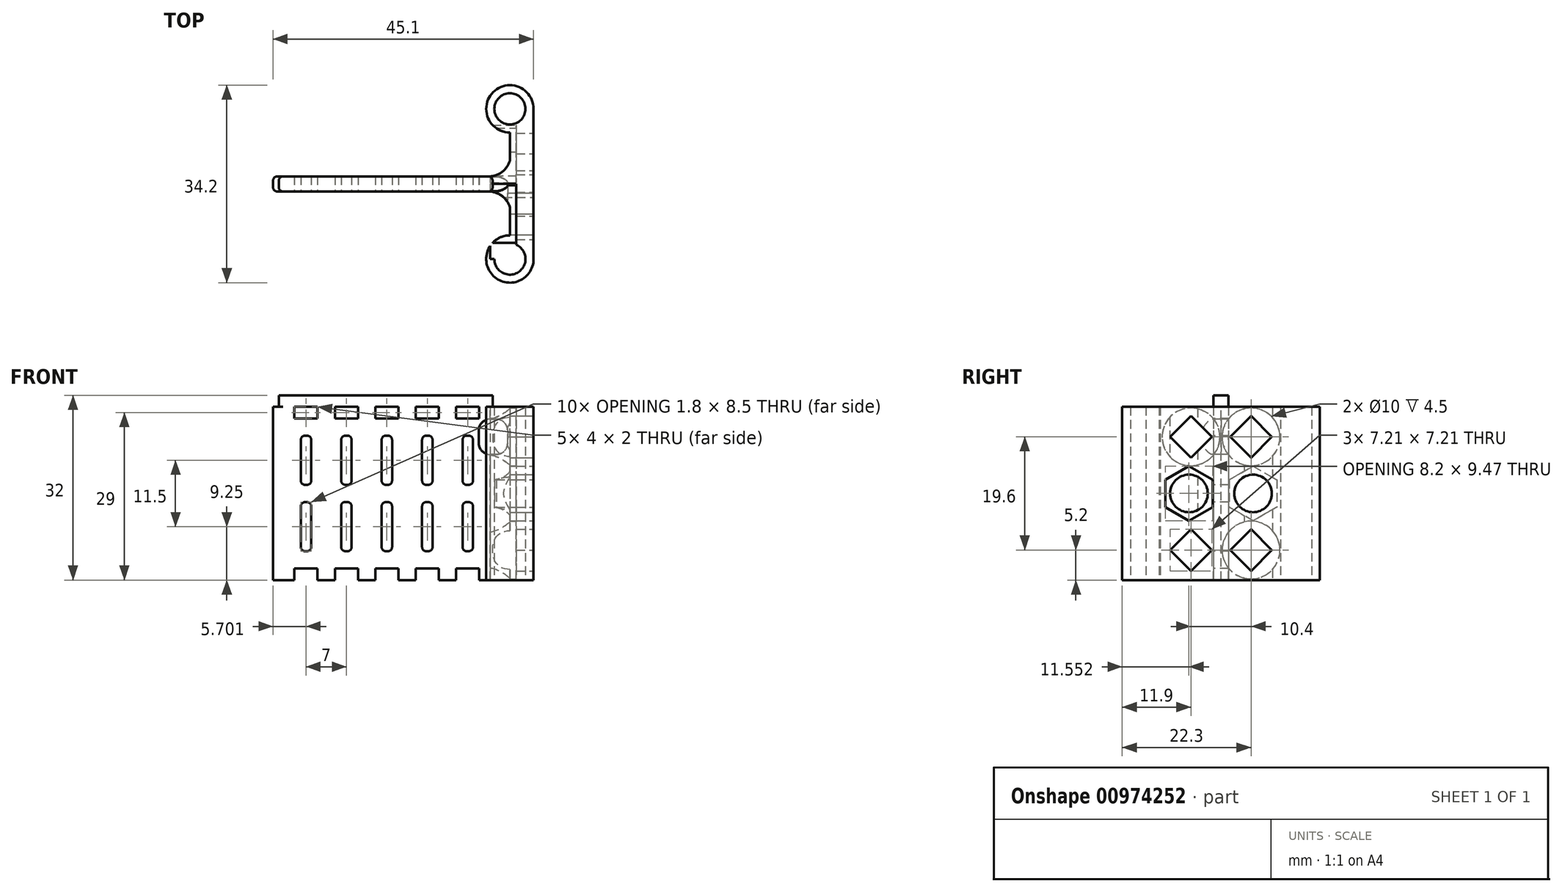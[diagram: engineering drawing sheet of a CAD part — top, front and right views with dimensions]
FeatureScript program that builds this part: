
annotation { "Feature Type Name" : "Feature", "Feature Type Description" : "" }
export const myFeature = defineFeature(function(context is Context, id is Id, definition is map)
    precondition{}
    {
        {
            var Q0;
            Q0=qCreatedBy(makeId("Top.planeOp"),FACE);
            var sketch = newSketch(context, id + "F0", { "sketchPlane" : qUnion([Q0])});
            skLineSegment(sketch, "E0", {"start": v(14.18, 21.66) * mm, "end": v(14.18, -4.34) * mm, "construction": true});
            skPoint(sketch, "E1", {"position": v(14.18, 8.66) * mm});
            skCircle(sketch, "E2", {"center": v(14.18, 21.66) * mm, "radius": 2.7 * mm});
            skCircle(sketch, "E3", {"center": v(14.18, -4.34) * mm, "radius": 2.7 * mm});
            skCircle(sketch, "E4", {"center": v(14.18, 21.66) * mm, "radius": 4.1 * mm});
            skCircle(sketch, "E5", {"center": v(14.18, -4.34) * mm, "radius": 4.1 * mm});
            skLineSegment(sketch, "E6", {"start": v(14.18, 26.11) * mm, "end": v(14.18, -8.89) * mm, "construction": true});
            skLineSegment(sketch, "E7", {"start": v(-25.82, 8.66) * mm, "end": v(11.18, 8.66) * mm, "construction": true});
            skLineSegment(sketch, "E8.0", {"start": v(-25.12, 7.36) * mm, "end": v(10.48, 7.36) * mm});
            skLineSegment(sketch, "E9.0", {"start": v(-25.12, 9.96) * mm, "end": v(10.48, 9.96) * mm});
            skLineSegment(sketch, "E10", {"start": v(-25.82, 9.26) * mm, "end": v(-25.82, 8.06) * mm});
            skLineSegment(sketch, "E11", {"start": v(11.18, 9.26) * mm, "end": v(11.18, 8.06) * mm});
            skLineSegment(sketch, "E12", {"start": v(11.18, 8.66) * mm, "end": v(14.18, 8.66) * mm, "construction": true});
            skPoint(sketch, "E13.visualSharp", {"position": v(11.18, 9.96) * mm});
            skArc(sketch, "E13.filletArc", {"start": v(11.18, 9.26) * mm, "mid": v(10.98, 9.76) * mm, "end": v(10.48, 9.96) * mm});
            skPoint(sketch, "E14.visualSharp", {"position": v(11.18, 7.36) * mm});
            skArc(sketch, "E14.filletArc", {"start": v(10.48, 7.36) * mm, "mid": v(10.98, 7.57) * mm, "end": v(11.18, 8.06) * mm});
            skPoint(sketch, "E15.visualSharp", {"position": v(-25.82, 9.96) * mm});
            skArc(sketch, "E15.filletArc", {"start": v(-25.12, 9.96) * mm, "mid": v(-25.61, 9.76) * mm, "end": v(-25.82, 9.26) * mm});
            skPoint(sketch, "E16.visualSharp", {"position": v(-25.82, 7.36) * mm});
            skArc(sketch, "E16.filletArc", {"start": v(-25.82, 8.06) * mm, "mid": v(-25.61, 7.57) * mm, "end": v(-25.12, 7.36) * mm});
            skLineSegment(sketch, "E17", {"start": v(18.28, 21.66) * mm, "end": v(18.28, -4.34) * mm});
            skLineSegment(sketch, "E18", {"start": v(14.18, 17.56) * mm, "end": v(14.18, -0.24) * mm});
            skPoint(sketch, "E19.startSnap0", {"position": v(13.1, 10.4) * mm});
            skArc(sketch, "E20", {"start": v(14.18, 4.62) * mm, "mid": v(12.78, 6.6) * mm, "end": v(10.48, 7.36) * mm});
            skArc(sketch, "E21.MirrorCS", {"start": v(14.18, 12.7) * mm, "mid": v(12.78, 10.72) * mm, "end": v(10.48, 9.96) * mm});
            skLineSegment(sketch, "E22.0", {"start": v(-26.82, 9.26) * mm, "end": v(-26.82, 8.06) * mm});
            skLineSegment(sketch, "E23", {"start": v(-25.12, 7.36) * mm, "end": v(-26.12, 7.36) * mm});
            skLineSegment(sketch, "E24", {"start": v(-25.12, 9.96) * mm, "end": v(-26.12, 9.96) * mm});
            skPoint(sketch, "E25.visualSharp", {"position": v(-26.82, 7.36) * mm});
            skArc(sketch, "E25.filletArc", {"start": v(-26.82, 8.06) * mm, "mid": v(-26.61, 7.57) * mm, "end": v(-26.12, 7.36) * mm});
            skPoint(sketch, "E26.visualSharp", {"position": v(-26.82, 9.96) * mm});
            skArc(sketch, "E26.filletArc", {"start": v(-26.12, 9.96) * mm, "mid": v(-26.61, 9.76) * mm, "end": v(-26.82, 9.26) * mm});
            skSolve(sketch);
        }
        {
            var Q0;
            Q0=qSketchRegion(id+"F0",true);
            extrude(context, id + "F1", {"entities" : qUnion([Q0]), "depth" : 30 * mm, "offsetDistance" : 25 * mm});
        }
        {
            var Q0;
            Q0=makeQuery(id+"F1.opExtrude","CAP_FACE",FACE,{"disambiguationData":[OSD([sQuery(id+"F0.wireOp",EDGE,"E2"),sQuery(id+"F0.wireOp",EDGE,"E3"),sQuery(id+"F0.wireOp",EDGE,"E4"),sQuery(id+"F0.wireOp",EDGE,"E5"),sQuery(id+"F0.wireOp",EDGE,"5XY8Sy6J-rJSc-VVxI-sy8d-kj6zddSfZvcS"),sQuery(id+"F0.wireOp",EDGE,"L47yK2bG-XMTy-tZuv-y9jX-F6sUyB3i6wNF"),sQuery(id+"F0.wireOp",EDGE,"E8.0"),sQuery(id+"F0.wireOp",EDGE,"E9.0"),sQuery(id+"F0.wireOp",EDGE,"E10"),sQuery(id+"F0.wireOp",EDGE,"E15.filletArc"),sQuery(id+"F0.wireOp",EDGE,"E16.filletArc"),sQuery(id+"F0.wireOp",EDGE,"fYA9DaEY-N4rZ-RQXs-IzNy-WeN906tYVGf5"),sQuery(id+"F0.wireOp",EDGE,"5c931c3b-5688-4883-9c1d-30dd6726151f0.MirrorCS")])],"isStart":false});
            var sketch = newSketch(context, id + "F2", { "sketchPlane" : qUnion([Q0])});
            skArc(sketch, "E27.0", {"start": v(11.18, 9.26) * mm, "mid": v(10.98, 9.76) * mm, "end": v(10.48, 9.96) * mm});
            skLineSegment(sketch, "E27.1", {"start": v(11.18, 9.26) * mm, "end": v(11.18, 8.06) * mm});
            skArc(sketch, "E27.2", {"start": v(10.48, 7.36) * mm, "mid": v(10.98, 7.57) * mm, "end": v(11.18, 8.06) * mm});
            skLineSegment(sketch, "E27.3", {"start": v(-25.12, 7.36) * mm, "end": v(10.48, 7.36) * mm});
            skLineSegment(sketch, "E27.4", {"start": v(-25.12, 9.96) * mm, "end": v(10.48, 9.96) * mm});
            skArc(sketch, "E27.5", {"start": v(-25.12, 9.96) * mm, "mid": v(-25.61, 9.76) * mm, "end": v(-25.82, 9.26) * mm});
            skLineSegment(sketch, "E27.6", {"start": v(-25.82, 9.26) * mm, "end": v(-25.82, 8.06) * mm});
            skArc(sketch, "E27.7", {"start": v(-25.82, 8.06) * mm, "mid": v(-25.61, 7.57) * mm, "end": v(-25.12, 7.36) * mm});
            skSolve(sketch);
        }
        {
            var Q0;
            Q0=makeQuery(id+"F2.imprint","IMPRINT",FACE,{"disambiguationData":[TD([[makeQuery(id+"F2.imprint","IMPRINT",EDGE,{"derivedFrom":sQuery(id+"F2.wireOp",EDGE,"E27.0")}),1.0]])]});
            extrude(context, id + "F3", {"entities" : qUnion([Q0]), "operationType" : NewBodyOperationType.ADD, "depth" : 2 * mm, "offsetDistance" : 25 * mm});
        }
        {
            var Q0;
            Q0=makeQuery(id+"F1.opExtrude","SWEPT_FACE",FACE,{"disambiguationData":[OSD([sQuery(id+"F0.wireOp",EDGE,"E17")])]});
            var sketch = newSketch(context, id + "F4", { "sketchPlane" : qUnion([Q0])});
            skCircle(sketch, "E28", {"center": v(14.2, 15) * mm, "radius": 3.25 * mm});
            skCircle(sketch, "E29.cCircle", {"center": v(14.2, 15) * mm, "radius": 4.1 * mm, "construction": true});
            skLineSegment(sketch, "E29.0", {"start": v(10.1, 12.63) * mm, "end": v(10.1, 17.37) * mm});
            skLineSegment(sketch, "E29.1", {"start": v(10.1, 17.37) * mm, "end": v(14.2, 19.74) * mm});
            skLineSegment(sketch, "E29.2", {"start": v(14.2, 19.74) * mm, "end": v(18.3, 17.37) * mm});
            skLineSegment(sketch, "E29.3", {"start": v(18.3, 17.37) * mm, "end": v(18.3, 12.63) * mm});
            skLineSegment(sketch, "E29.4", {"start": v(18.3, 12.63) * mm, "end": v(14.2, 10.27) * mm});
            skLineSegment(sketch, "E29.5", {"start": v(14.2, 10.27) * mm, "end": v(10.1, 12.63) * mm});
            skPoint(sketch, "E29.0.midPoint", {"position": v(10.1, 15) * mm});
            skCircle(sketch, "E30", {"center": v(13.86, 24.8) * mm, "radius": 5 * mm});
            skLineSegment(sketch, "E31", {"start": v(8.66, 0) * mm, "end": v(8.66, 30) * mm});
            skLineSegment(sketch, "E32.bottom", {"start": v(17.47, 24.8) * mm, "end": v(13.86, 28.4) * mm});
            skLineSegment(sketch, "E32.top", {"start": v(13.86, 21.2) * mm, "end": v(10.25, 24.8) * mm});
            skLineSegment(sketch, "E32.left", {"start": v(17.47, 24.8) * mm, "end": v(13.86, 21.2) * mm});
            skLineSegment(sketch, "E32.right", {"start": v(13.86, 28.4) * mm, "end": v(10.25, 24.8) * mm});
            skCircle(sketch, "E33.MirrorC", {"center": v(3.46, 24.8) * mm, "radius": 5 * mm});
            skLineSegment(sketch, "E34.MirrorCS", {"start": v(3.46, 28.4) * mm, "end": v(7.07, 24.8) * mm});
            skLineSegment(sketch, "E35.MirrorCS", {"start": v(-0.15, 24.8) * mm, "end": v(3.46, 21.2) * mm});
            skLineSegment(sketch, "E36.MirrorCS", {"start": v(3.46, 21.2) * mm, "end": v(7.07, 24.8) * mm});
            skLineSegment(sketch, "E37.MirrorCS", {"start": v(-0.15, 24.8) * mm, "end": v(3.46, 28.4) * mm});
            skLineSegment(sketch, "E38.MirrorCS", {"start": v(3.11, 10.27) * mm, "end": v(7.21, 12.63) * mm});
            skLineSegment(sketch, "E39.MirrorCS", {"start": v(3.11, 19.74) * mm, "end": v(-0.99, 17.37) * mm});
            skLineSegment(sketch, "E40.MirrorCS", {"start": v(-0.99, 12.63) * mm, "end": v(3.11, 10.27) * mm});
            skPoint(sketch, "E41.MirrorP", {"position": v(7.21, 15) * mm});
            skLineSegment(sketch, "E42.MirrorCS", {"start": v(7.21, 17.37) * mm, "end": v(3.11, 19.74) * mm});
            skLineSegment(sketch, "E43.MirrorCS", {"start": v(7.21, 12.63) * mm, "end": v(7.21, 17.37) * mm});
            skLineSegment(sketch, "E44.MirrorCS", {"start": v(-0.99, 17.37) * mm, "end": v(-0.99, 12.63) * mm});
            skCircle(sketch, "E45.MirrorC", {"center": v(3.11, 15) * mm, "radius": 4.1 * mm, "construction": true});
            skCircle(sketch, "E46.MirrorC", {"center": v(3.11, 15) * mm, "radius": 3.25 * mm});
            skLineSegment(sketch, "E47", {"start": v(13.86, 30) * mm, "end": v(13.86, 0) * mm, "construction": true});
            skLineSegment(sketch, "E48", {"start": v(-4.34, 15) * mm, "end": v(21.66, 15) * mm, "construction": true});
            skLineSegment(sketch, "E49.MirrorCS", {"start": v(17.47, 5.2) * mm, "end": v(13.86, 1.6) * mm});
            skLineSegment(sketch, "E50.MirrorCS", {"start": v(-0.15, 5.2) * mm, "end": v(3.46, 1.6) * mm});
            skPoint(sketch, "E51.MirrorP", {"position": v(3.46, 5.2) * mm});
            skCircle(sketch, "E52.MirrorC", {"center": v(3.46, 5.2) * mm, "radius": 5 * mm});
            skLineSegment(sketch, "E53.MirrorCS", {"start": v(17.47, 5.2) * mm, "end": v(13.86, 8.8) * mm});
            skLineSegment(sketch, "E54.MirrorCS", {"start": v(13.86, 8.8) * mm, "end": v(10.25, 5.2) * mm});
            skLineSegment(sketch, "E55.MirrorCS", {"start": v(3.46, 1.6) * mm, "end": v(7.07, 5.2) * mm});
            skPoint(sketch, "E56.MirrorP", {"position": v(13.86, 5.2) * mm});
            skCircle(sketch, "E57.MirrorC", {"center": v(13.86, 5.2) * mm, "radius": 5 * mm});
            skLineSegment(sketch, "E58.MirrorCS", {"start": v(-0.15, 5.2) * mm, "end": v(3.46, 8.8) * mm});
            skLineSegment(sketch, "E59.MirrorCS", {"start": v(3.46, 8.8) * mm, "end": v(7.07, 5.2) * mm});
            skLineSegment(sketch, "E60.MirrorCS", {"start": v(13.86, 1.6) * mm, "end": v(10.25, 5.2) * mm});
            skSolve(sketch);
        }
        {
            var Q0;
            Q0=makeQuery(id+"F4.imprint","IMPRINT",FACE,{"disambiguationData":[TD([[makeQuery(id+"F4.imprint","IMPRINT",EDGE,{"derivedFrom":sQuery(id+"F4.wireOp",EDGE,"E28")}),1.0]])]});
            var Q1;
            Q1=makeQuery(id+"F4.imprint","IMPRINT",FACE,{"disambiguationData":[TD([[makeQuery(id+"F4.imprint","IMPRINT",EDGE,{"derivedFrom":sQuery(id+"F4.wireOp",EDGE,"E34.MirrorCS")}),-1.0]])]});
            var Q2;
            Q2=makeQuery(id+"F4.imprint","IMPRINT",FACE,{"disambiguationData":[TD([[makeQuery(id+"F4.imprint","IMPRINT",EDGE,{"derivedFrom":sQuery(id+"F4.wireOp",EDGE,"E32.bottom")}),1.0]])]});
            var Q3;
            Q3=makeQuery(id+"F4.imprint","IMPRINT",FACE,{"disambiguationData":[TD([[makeQuery(id+"F4.imprint","IMPRINT",EDGE,{"derivedFrom":sQuery(id+"F4.wireOp",EDGE,"E46.MirrorC")}),-1.0]])]});
            var Q4;
            Q4=makeQuery(id+"F4.imprint","IMPRINT",FACE,{"disambiguationData":[TD([[makeQuery(id+"F4.imprint","IMPRINT",EDGE,{"derivedFrom":sQuery(id+"F4.wireOp",EDGE,"E50.MirrorCS")}),1.0]])]});
            var Q5;
            Q5=makeQuery(id+"F4.imprint","IMPRINT",FACE,{"disambiguationData":[TD([[makeQuery(id+"F4.imprint","IMPRINT",EDGE,{"derivedFrom":sQuery(id+"F4.wireOp",EDGE,"E49.MirrorCS")}),-1.0]])]});
            extrude(context, id + "F5", {"entities" : qUnion([Q0, Q1, Q2, Q3, Q4, Q5]), "operationType" : NewBodyOperationType.REMOVE, "oppositeDirection" : true, "depth" : 25 * mm, "offsetDistance" : 25 * mm});
        }
        {
            var Q0;
            Q0=makeQuery(id+"F4.imprint","IMPRINT",FACE,{"disambiguationData":[TD([[makeQuery(id+"F4.imprint","IMPRINT",EDGE,{"derivedFrom":sQuery(id+"F4.wireOp",EDGE,"E28")}),-1.0]])]});
            var Q1;
            Q1=makeQuery(id+"F4.imprint","IMPRINT",FACE,{"disambiguationData":[TD([[makeQuery(id+"F4.imprint","IMPRINT",EDGE,{"derivedFrom":sQuery(id+"F4.wireOp",EDGE,"E33.MirrorC")}),-1.0]])]});
            var Q2;
            Q2=makeQuery(id+"F4.imprint","IMPRINT",FACE,{"disambiguationData":[TD([[makeQuery(id+"F4.imprint","IMPRINT",EDGE,{"derivedFrom":sQuery(id+"F4.wireOp",EDGE,"E30")}),1.0]])]});
            var Q3;
            Q3=makeQuery(id+"F4.imprint","IMPRINT",FACE,{"disambiguationData":[TD([[makeQuery(id+"F4.imprint","IMPRINT",EDGE,{"derivedFrom":sQuery(id+"F4.wireOp",EDGE,"E38.MirrorCS")}),1.0]])]});
            var Q4;
            Q4=makeQuery(id+"F4.imprint","IMPRINT",FACE,{"disambiguationData":[TD([[makeQuery(id+"F4.imprint","IMPRINT",EDGE,{"derivedFrom":sQuery(id+"F4.wireOp",EDGE,"E50.MirrorCS")}),-1.0]])]});
            var Q5;
            Q5=makeQuery(id+"F4.imprint","IMPRINT",FACE,{"disambiguationData":[TD([[makeQuery(id+"F4.imprint","IMPRINT",EDGE,{"derivedFrom":sQuery(id+"F4.wireOp",EDGE,"E49.MirrorCS")}),1.0]])]});
            extrude(context, id + "F6", {"entities" : qUnion([Q0, Q1, Q2, Q3, Q4, Q5]), "operationType" : NewBodyOperationType.REMOVE, "oppositeDirection" : true, "depth" : 7.5 * mm, "offsetDistance" : 25 * mm, "hasSecondDirection" : true, "secondDirectionOppositeDirection" : true, "secondDirectionDepth" : 3 * mm});
        }
        {
            var Q0;
            Q0=makeQuery(id+"F3.boolean.opBoolean","MERGE",FACE,{"derivedFrom":[makeQuery(id+"F1.opExtrude","SWEPT_FACE",FACE,{"disambiguationData":[OSD([sQuery(id+"F0.wireOp",EDGE,"E8.0")])]}),makeQuery(id+"F3.opExtrude","SWEPT_FACE",FACE,{"disambiguationData":[OSD([sQuery(id+"F2.wireOp",EDGE,"E27.3")])]})]});
            var sketch = newSketch(context, id + "F7", { "sketchPlane" : qUnion([Q0])});
            skLineSegment(sketch, "E61", {"start": v(10.48, 0) * mm, "end": v(10.48, 0) * mm});
            skPoint(sketch, "E62.startSnap0", {"position": v(1.88, 12.72) * mm});
            skPoint(sketch, "E63.startSnap0", {"position": v(4.88, 13.72) * mm});
            skLineSegment(sketch, "E64.bottom", {"start": v(7.08, 25) * mm, "end": v(6.68, 25) * mm});
            skLineSegment(sketch, "E64.top", {"start": v(7.08, 5) * mm, "end": v(6.68, 5) * mm});
            skLineSegment(sketch, "E64.left", {"start": v(7.78, 24.3) * mm, "end": v(7.78, 17.2) * mm});
            skLineSegment(sketch, "E64.right", {"start": v(5.98, 24.3) * mm, "end": v(5.98, 17.2) * mm});
            skPoint(sketch, "E64.middle", {"position": v(6.88, 15) * mm});
            skPoint(sketch, "E64.middle.positionSnap0", {"position": v(-26.12, 15) * mm});
            skPoint(sketch, "E64.middle.positionSnap1", {"position": v(6.88, 12.18) * mm});
            skPoint(sketch, "E64.centerSnap0", {"position": v(-26.12, 15) * mm});
            skPoint(sketch, "E64.centerSnap1", {"position": v(6.88, 12.18) * mm});
            skLineSegment(sketch, "E65.bottom", {"start": v(-0.32, 25) * mm, "end": v(0.08, 25) * mm});
            skLineSegment(sketch, "E65.top", {"start": v(-0.32, 5) * mm, "end": v(0.08, 5) * mm});
            skLineSegment(sketch, "E65.left", {"start": v(-1.02, 24.3) * mm, "end": v(-1.02, 17.2) * mm});
            skLineSegment(sketch, "E65.right", {"start": v(0.78, 24.3) * mm, "end": v(0.78, 17.2) * mm});
            skPoint(sketch, "E65.middle", {"position": v(-0.12, 15) * mm});
            skPoint(sketch, "E65.middle.positionSnap0", {"position": v(7.78, 15) * mm});
            skPoint(sketch, "E65.middle.positionSnap1", {"position": v(-0.12, 10.92) * mm});
            skPoint(sketch, "E65.centerSnap0", {"position": v(7.78, 15) * mm});
            skPoint(sketch, "E65.centerSnap1", {"position": v(-0.12, 10.92) * mm});
            skLineSegment(sketch, "E66.bottom", {"start": v(-6.92, 25) * mm, "end": v(-7.32, 25) * mm});
            skLineSegment(sketch, "E66.top", {"start": v(-6.92, 5) * mm, "end": v(-7.32, 5) * mm});
            skLineSegment(sketch, "E66.left", {"start": v(-6.22, 24.3) * mm, "end": v(-6.22, 17.2) * mm});
            skLineSegment(sketch, "E66.right", {"start": v(-8.02, 24.3) * mm, "end": v(-8.02, 17.2) * mm});
            skPoint(sketch, "E66.middle", {"position": v(-7.12, 15) * mm});
            skPoint(sketch, "E66.middle.positionSnap0", {"position": v(0.78, 15) * mm});
            skPoint(sketch, "E66.centerSnap0", {"position": v(0.78, 15) * mm});
            skLineSegment(sketch, "E67.bottom", {"start": v(-13.92, 25) * mm, "end": v(-14.32, 25) * mm});
            skLineSegment(sketch, "E67.top", {"start": v(-13.92, 5) * mm, "end": v(-14.32, 5) * mm});
            skLineSegment(sketch, "E67.left", {"start": v(-13.22, 24.3) * mm, "end": v(-13.22, 17.2) * mm});
            skLineSegment(sketch, "E67.right", {"start": v(-15.02, 24.3) * mm, "end": v(-15.02, 17.2) * mm});
            skPoint(sketch, "E67.middle", {"position": v(-14.12, 15) * mm});
            skPoint(sketch, "E67.middle.positionSnap0", {"position": v(-6.22, 15) * mm});
            skPoint(sketch, "E67.centerSnap0", {"position": v(-6.22, 15) * mm});
            skLineSegment(sketch, "E68.bottom", {"start": v(-20.92, 25) * mm, "end": v(-21.32, 25) * mm});
            skLineSegment(sketch, "E68.top", {"start": v(-20.92, 5) * mm, "end": v(-21.32, 5) * mm});
            skLineSegment(sketch, "E68.left", {"start": v(-20.22, 24.3) * mm, "end": v(-20.22, 17.2) * mm});
            skLineSegment(sketch, "E68.right", {"start": v(-22.02, 24.3) * mm, "end": v(-22.02, 17.2) * mm});
            skPoint(sketch, "E68.middle", {"position": v(-21.12, 15) * mm});
            skPoint(sketch, "E68.middle.positionSnap0", {"position": v(-13.22, 15) * mm});
            skPoint(sketch, "E68.centerSnap0", {"position": v(-13.22, 15) * mm});
            skPoint(sketch, "E69.visualSharp", {"position": v(5.98, 25) * mm});
            skArc(sketch, "E69.filletArc", {"start": v(6.68, 25) * mm, "mid": v(6.19, 24.8) * mm, "end": v(5.98, 24.3) * mm});
            skPoint(sketch, "E70.visualSharp", {"position": v(7.78, 25) * mm});
            skArc(sketch, "E70.filletArc", {"start": v(7.78, 24.3) * mm, "mid": v(7.58, 24.8) * mm, "end": v(7.08, 25) * mm});
            skPoint(sketch, "E71.visualSharp", {"position": v(5.98, 5) * mm});
            skArc(sketch, "E71.filletArc", {"start": v(5.98, 5.7) * mm, "mid": v(6.19, 5.2) * mm, "end": v(6.68, 5) * mm});
            skPoint(sketch, "E72.visualSharp", {"position": v(7.78, 5) * mm});
            skArc(sketch, "E72.filletArc", {"start": v(7.08, 5) * mm, "mid": v(7.58, 5.2) * mm, "end": v(7.78, 5.7) * mm});
            skPoint(sketch, "E73.visualSharp", {"position": v(-1.02, 5) * mm});
            skArc(sketch, "E73.filletArc", {"start": v(-1.02, 5.7) * mm, "mid": v(-0.81, 5.2) * mm, "end": v(-0.32, 5) * mm});
            skPoint(sketch, "E74.visualSharp", {"position": v(-1.02, 25) * mm});
            skArc(sketch, "E74.filletArc", {"start": v(-0.32, 25) * mm, "mid": v(-0.81, 24.8) * mm, "end": v(-1.02, 24.3) * mm});
            skPoint(sketch, "E75.visualSharp", {"position": v(0.78, 5) * mm});
            skArc(sketch, "E75.filletArc", {"start": v(0.08, 5) * mm, "mid": v(0.58, 5.2) * mm, "end": v(0.78, 5.7) * mm});
            skPoint(sketch, "E76.visualSharp", {"position": v(0.78, 25) * mm});
            skArc(sketch, "E76.filletArc", {"start": v(0.78, 24.3) * mm, "mid": v(0.58, 24.8) * mm, "end": v(0.08, 25) * mm});
            skPoint(sketch, "E77.visualSharp", {"position": v(-8.02, 25) * mm});
            skArc(sketch, "E77.filletArc", {"start": v(-7.32, 25) * mm, "mid": v(-7.81, 24.8) * mm, "end": v(-8.02, 24.3) * mm});
            skPoint(sketch, "E78.visualSharp", {"position": v(-8.02, 5) * mm});
            skArc(sketch, "E78.filletArc", {"start": v(-8.02, 5.7) * mm, "mid": v(-7.81, 5.2) * mm, "end": v(-7.32, 5) * mm});
            skPoint(sketch, "E79.visualSharp", {"position": v(-6.22, 25) * mm});
            skArc(sketch, "E79.filletArc", {"start": v(-6.22, 24.3) * mm, "mid": v(-6.42, 24.8) * mm, "end": v(-6.92, 25) * mm});
            skPoint(sketch, "E80.visualSharp", {"position": v(-6.22, 5) * mm});
            skArc(sketch, "E80.filletArc", {"start": v(-6.92, 5) * mm, "mid": v(-6.42, 5.2) * mm, "end": v(-6.22, 5.7) * mm});
            skPoint(sketch, "E81.visualSharp", {"position": v(-15.02, 5) * mm});
            skArc(sketch, "E81.filletArc", {"start": v(-15.02, 5.7) * mm, "mid": v(-14.81, 5.2) * mm, "end": v(-14.32, 5) * mm});
            skPoint(sketch, "E82.visualSharp", {"position": v(-15.02, 25) * mm});
            skArc(sketch, "E82.filletArc", {"start": v(-14.32, 25) * mm, "mid": v(-14.81, 24.8) * mm, "end": v(-15.02, 24.3) * mm});
            skPoint(sketch, "E83.visualSharp", {"position": v(-13.22, 5) * mm});
            skArc(sketch, "E83.filletArc", {"start": v(-13.92, 5) * mm, "mid": v(-13.42, 5.2) * mm, "end": v(-13.22, 5.7) * mm});
            skPoint(sketch, "E84.visualSharp", {"position": v(-13.22, 25) * mm});
            skArc(sketch, "E84.filletArc", {"start": v(-13.22, 24.3) * mm, "mid": v(-13.42, 24.8) * mm, "end": v(-13.92, 25) * mm});
            skPoint(sketch, "E85.visualSharp", {"position": v(-22.02, 25) * mm});
            skArc(sketch, "E85.filletArc", {"start": v(-21.32, 25) * mm, "mid": v(-21.81, 24.8) * mm, "end": v(-22.02, 24.3) * mm});
            skPoint(sketch, "E86.visualSharp", {"position": v(-22.02, 5) * mm});
            skArc(sketch, "E86.filletArc", {"start": v(-22.02, 5.7) * mm, "mid": v(-21.81, 5.2) * mm, "end": v(-21.32, 5) * mm});
            skPoint(sketch, "E87.visualSharp", {"position": v(-20.22, 25) * mm});
            skArc(sketch, "E87.filletArc", {"start": v(-20.22, 24.3) * mm, "mid": v(-20.42, 24.8) * mm, "end": v(-20.92, 25) * mm});
            skPoint(sketch, "E88.visualSharp", {"position": v(-20.22, 5) * mm});
            skArc(sketch, "E88.filletArc", {"start": v(-20.92, 5) * mm, "mid": v(-20.42, 5.2) * mm, "end": v(-20.22, 5.7) * mm});
            skLineSegment(sketch, "E89", {"start": v(-26.12, 15) * mm, "end": v(10.48, 15) * mm, "construction": true});
            skLineSegment(sketch, "E90.bottom", {"start": v(-19.12, 0) * mm, "end": v(-23.12, 0) * mm});
            skLineSegment(sketch, "E90.top", {"start": v(-19.12, 2) * mm, "end": v(-23.12, 2) * mm});
            skLineSegment(sketch, "E90.left", {"start": v(-19.12, 0) * mm, "end": v(-19.12, 2) * mm});
            skLineSegment(sketch, "E90.right", {"start": v(-23.12, 0) * mm, "end": v(-23.12, 2) * mm});
            skPoint(sketch, "E90.middle", {"position": v(-21.12, 1) * mm});
            skLineSegment(sketch, "E91.bottom", {"start": v(-12.12, 0) * mm, "end": v(-16.12, 0) * mm});
            skLineSegment(sketch, "E91.top", {"start": v(-12.12, 2) * mm, "end": v(-16.12, 2) * mm});
            skLineSegment(sketch, "E91.left", {"start": v(-12.12, 0) * mm, "end": v(-12.12, 2) * mm});
            skLineSegment(sketch, "E91.right", {"start": v(-16.12, 0) * mm, "end": v(-16.12, 2) * mm});
            skPoint(sketch, "E91.middle", {"position": v(-14.12, 1) * mm});
            skLineSegment(sketch, "E92.bottom", {"start": v(-5.12, 0) * mm, "end": v(-9.12, 0) * mm});
            skLineSegment(sketch, "E92.top", {"start": v(-5.12, 2) * mm, "end": v(-9.12, 2) * mm});
            skLineSegment(sketch, "E92.left", {"start": v(-5.12, 0) * mm, "end": v(-5.12, 2) * mm});
            skLineSegment(sketch, "E92.right", {"start": v(-9.12, 0) * mm, "end": v(-9.12, 2) * mm});
            skPoint(sketch, "E92.middle", {"position": v(-7.12, 1) * mm});
            skLineSegment(sketch, "E93.bottom", {"start": v(1.88, 0) * mm, "end": v(-2.12, 0) * mm});
            skLineSegment(sketch, "E93.top", {"start": v(1.88, 2) * mm, "end": v(-2.12, 2) * mm});
            skLineSegment(sketch, "E93.left", {"start": v(1.88, 0) * mm, "end": v(1.88, 2) * mm});
            skLineSegment(sketch, "E93.right", {"start": v(-2.12, 0) * mm, "end": v(-2.12, 2) * mm});
            skPoint(sketch, "E93.middle", {"position": v(-0.12, 1) * mm});
            skLineSegment(sketch, "E94.bottom", {"start": v(8.88, 0) * mm, "end": v(4.88, 0) * mm});
            skLineSegment(sketch, "E94.top", {"start": v(8.88, 2) * mm, "end": v(4.88, 2) * mm});
            skLineSegment(sketch, "E94.left", {"start": v(8.88, 0) * mm, "end": v(8.88, 2) * mm});
            skLineSegment(sketch, "E94.right", {"start": v(4.88, 0) * mm, "end": v(4.88, 2) * mm});
            skPoint(sketch, "E94.middle", {"position": v(6.88, 1) * mm});
            skLineSegment(sketch, "E95.MirrorCS", {"start": v(1.88, 30) * mm, "end": v(1.88, 28) * mm});
            skLineSegment(sketch, "E96.MirrorCS", {"start": v(-16.12, 30) * mm, "end": v(-16.12, 28) * mm});
            skLineSegment(sketch, "E97.MirrorCS", {"start": v(-12.12, 30) * mm, "end": v(-16.12, 30) * mm});
            skLineSegment(sketch, "E98.MirrorCS", {"start": v(-12.12, 30) * mm, "end": v(-12.12, 28) * mm});
            skLineSegment(sketch, "E99.MirrorCS", {"start": v(4.88, 30) * mm, "end": v(4.88, 28) * mm});
            skLineSegment(sketch, "E100.MirrorCS", {"start": v(-2.12, 30) * mm, "end": v(-2.12, 28) * mm});
            skLineSegment(sketch, "E101.MirrorCS", {"start": v(-19.12, 30) * mm, "end": v(-19.12, 28) * mm});
            skLineSegment(sketch, "E102.MirrorCS", {"start": v(-12.12, 28) * mm, "end": v(-16.12, 28) * mm});
            skLineSegment(sketch, "E103.MirrorCS", {"start": v(-23.12, 30) * mm, "end": v(-23.12, 28) * mm});
            skPoint(sketch, "E104.MirrorP", {"position": v(-14.12, 29) * mm});
            skLineSegment(sketch, "E105.MirrorCS", {"start": v(-19.12, 30) * mm, "end": v(-23.12, 30) * mm});
            skLineSegment(sketch, "E106.MirrorCS", {"start": v(-19.12, 28) * mm, "end": v(-23.12, 28) * mm});
            skPoint(sketch, "E107.MirrorP", {"position": v(-0.12, 29) * mm});
            skLineSegment(sketch, "E108.MirrorCS", {"start": v(-9.12, 30) * mm, "end": v(-9.12, 28) * mm});
            skLineSegment(sketch, "E109.MirrorCS", {"start": v(-5.12, 30) * mm, "end": v(-9.12, 30) * mm});
            skPoint(sketch, "E110.MirrorP", {"position": v(6.88, 29) * mm});
            skLineSegment(sketch, "E111.MirrorCS", {"start": v(8.88, 28) * mm, "end": v(4.88, 28) * mm});
            skLineSegment(sketch, "E112.MirrorCS", {"start": v(-5.12, 30) * mm, "end": v(-5.12, 28) * mm});
            skLineSegment(sketch, "E113.MirrorCS", {"start": v(8.88, 30) * mm, "end": v(4.88, 30) * mm});
            skLineSegment(sketch, "E114.MirrorCS", {"start": v(1.88, 30) * mm, "end": v(-2.12, 30) * mm});
            skLineSegment(sketch, "E115.MirrorCS", {"start": v(-5.12, 28) * mm, "end": v(-9.12, 28) * mm});
            skLineSegment(sketch, "E116.MirrorCS", {"start": v(1.88, 28) * mm, "end": v(-2.12, 28) * mm});
            skLineSegment(sketch, "E117.MirrorCS", {"start": v(8.88, 30) * mm, "end": v(8.88, 28) * mm});
            skPoint(sketch, "E118.MirrorP", {"position": v(-7.12, 29) * mm});
            skPoint(sketch, "E119.MirrorP", {"position": v(-21.12, 29) * mm});
            skLineSegment(sketch, "E120.bottom", {"start": v(10.78, 27.88) * mm, "end": v(11.78, 27.88) * mm});
            skLineSegment(sketch, "E120.top", {"start": v(10.78, 21.75) * mm, "end": v(11.78, 21.75) * mm});
            skLineSegment(sketch, "E120.left", {"start": v(8.78, 25.88) * mm, "end": v(8.78, 23.75) * mm});
            skLineSegment(sketch, "E120.right", {"start": v(13.78, 25.88) * mm, "end": v(13.78, 23.75) * mm});
            skPoint(sketch, "E121.visualSharp", {"position": v(10.78, 21.66) * mm});
            skArc(sketch, "E121.filletArc", {"start": v(10.78, 27.88) * mm, "mid": v(9.37, 27.3) * mm, "end": v(8.78, 25.88) * mm});
            skPoint(sketch, "E122.visualSharp", {"position": v(10.78, 21.75) * mm});
            skArc(sketch, "E122.filletArc", {"start": v(8.78, 23.75) * mm, "mid": v(9.37, 22.34) * mm, "end": v(10.78, 21.75) * mm});
            skPoint(sketch, "E123.visualSharp", {"position": v(15.78, 27.88) * mm});
            skArc(sketch, "E123.filletArc", {"start": v(13.78, 25.88) * mm, "mid": v(13.2, 27.3) * mm, "end": v(11.78, 27.88) * mm});
            skPoint(sketch, "E124.visualSharp", {"position": v(15.78, 21.75) * mm});
            skArc(sketch, "E124.filletArc", {"start": v(11.78, 21.75) * mm, "mid": v(13.2, 22.34) * mm, "end": v(13.78, 23.75) * mm});
            skLineSegment(sketch, "E125", {"start": v(-21.32, 16.5) * mm, "end": v(-20.92, 16.5) * mm});
            skLineSegment(sketch, "E126.MirrorCS", {"start": v(-21.32, 13.5) * mm, "end": v(-20.92, 13.5) * mm});
            skLineSegment(sketch, "E127.trimOffspring", {"start": v(-22.02, 12.8) * mm, "end": v(-22.02, 5.7) * mm});
            skLineSegment(sketch, "E128.trimOffspring", {"start": v(-14.32, 16.5) * mm, "end": v(-13.92, 16.5) * mm});
            skLineSegment(sketch, "E129.trimOffspring", {"start": v(-14.42, 13.5) * mm, "end": v(-13.92, 13.5) * mm});
            skLineSegment(sketch, "E130.trimOffspring", {"start": v(-7.32, 13.5) * mm, "end": v(-6.92, 13.5) * mm});
            skLineSegment(sketch, "E131.trimOffspring", {"start": v(-0.32, 13.5) * mm, "end": v(0.08, 13.5) * mm});
            skLineSegment(sketch, "E132.trimOffspring", {"start": v(-0.32, 16.5) * mm, "end": v(0.08, 16.5) * mm});
            skLineSegment(sketch, "E133.trimOffspring", {"start": v(6.68, 16.5) * mm, "end": v(7.08, 16.5) * mm});
            skLineSegment(sketch, "E134.trimOffspring", {"start": v(6.68, 13.5) * mm, "end": v(7.08, 13.5) * mm});
            skLineSegment(sketch, "E135.trimOffspring", {"start": v(7.78, 12.8) * mm, "end": v(7.78, 5.7) * mm});
            skLineSegment(sketch, "E136.trimOffspring", {"start": v(5.98, 12.8) * mm, "end": v(5.98, 5.7) * mm});
            skLineSegment(sketch, "E137.trimOffspring", {"start": v(0.78, 12.8) * mm, "end": v(0.78, 5.7) * mm});
            skLineSegment(sketch, "E138.trimOffspring", {"start": v(-1.02, 12.8) * mm, "end": v(-1.02, 5.7) * mm});
            skLineSegment(sketch, "E139.trimOffspring", {"start": v(-13.22, 12.8) * mm, "end": v(-13.22, 5.7) * mm});
            skLineSegment(sketch, "E140.trimOffspring", {"start": v(-15.02, 12.9) * mm, "end": v(-15.02, 5.7) * mm});
            skLineSegment(sketch, "E141.trimOffspring", {"start": v(-20.22, 12.8) * mm, "end": v(-20.22, 5.7) * mm});
            skLineSegment(sketch, "E142.MirrorCS", {"start": v(-7.32, 16.5) * mm, "end": v(-6.92, 16.5) * mm});
            skLineSegment(sketch, "E143.trimOffspring", {"start": v(-8.02, 12.8) * mm, "end": v(-8.02, 5.7) * mm});
            skLineSegment(sketch, "E144.trimOffspring", {"start": v(-6.22, 12.8) * mm, "end": v(-6.22, 5.7) * mm});
            skPoint(sketch, "E145.visualSharp", {"position": v(-22.02, 16.5) * mm});
            skArc(sketch, "E145.filletArc", {"start": v(-22.02, 17.2) * mm, "mid": v(-21.81, 16.7) * mm, "end": v(-21.32, 16.5) * mm});
            skPoint(sketch, "E146.visualSharp", {"position": v(-20.22, 16.5) * mm});
            skArc(sketch, "E146.filletArc", {"start": v(-20.92, 16.5) * mm, "mid": v(-20.42, 16.7) * mm, "end": v(-20.22, 17.2) * mm});
            skPoint(sketch, "E147.visualSharp", {"position": v(-22.02, 13.5) * mm});
            skArc(sketch, "E147.filletArc", {"start": v(-21.32, 13.5) * mm, "mid": v(-21.81, 13.3) * mm, "end": v(-22.02, 12.8) * mm});
            skPoint(sketch, "E148.visualSharp", {"position": v(-20.22, 13.5) * mm});
            skArc(sketch, "E148.filletArc", {"start": v(-20.22, 12.8) * mm, "mid": v(-20.42, 13.3) * mm, "end": v(-20.92, 13.5) * mm});
            skPoint(sketch, "E149.visualSharp", {"position": v(-15.02, 16.5) * mm});
            skArc(sketch, "E149.filletArc", {"start": v(-15.02, 17.2) * mm, "mid": v(-14.81, 16.7) * mm, "end": v(-14.32, 16.5) * mm});
            skPoint(sketch, "E150.visualSharp", {"position": v(-15.02, 13.5) * mm});
            skArc(sketch, "E150.filletArc", {"start": v(-14.42, 13.5) * mm, "mid": v(-14.84, 13.32) * mm, "end": v(-15.02, 12.9) * mm});
            skPoint(sketch, "E151.visualSharp", {"position": v(-13.22, 16.5) * mm});
            skArc(sketch, "E151.filletArc", {"start": v(-13.92, 16.5) * mm, "mid": v(-13.42, 16.7) * mm, "end": v(-13.22, 17.2) * mm});
            skPoint(sketch, "E152.visualSharp", {"position": v(-13.22, 13.5) * mm});
            skArc(sketch, "E152.filletArc", {"start": v(-13.22, 12.8) * mm, "mid": v(-13.42, 13.3) * mm, "end": v(-13.92, 13.5) * mm});
            skPoint(sketch, "E153.visualSharp", {"position": v(-8.02, 16.5) * mm});
            skArc(sketch, "E153.filletArc", {"start": v(-8.02, 17.2) * mm, "mid": v(-7.81, 16.7) * mm, "end": v(-7.32, 16.5) * mm});
            skPoint(sketch, "E154.visualSharp", {"position": v(-8.02, 13.5) * mm});
            skArc(sketch, "E154.filletArc", {"start": v(-7.32, 13.5) * mm, "mid": v(-7.81, 13.3) * mm, "end": v(-8.02, 12.8) * mm});
            skPoint(sketch, "E155.visualSharp", {"position": v(-6.22, 13.5) * mm});
            skArc(sketch, "E155.filletArc", {"start": v(-6.22, 12.8) * mm, "mid": v(-6.42, 13.3) * mm, "end": v(-6.92, 13.5) * mm});
            skPoint(sketch, "E156.visualSharp", {"position": v(-6.22, 16.5) * mm});
            skArc(sketch, "E156.filletArc", {"start": v(-6.92, 16.5) * mm, "mid": v(-6.42, 16.7) * mm, "end": v(-6.22, 17.2) * mm});
            skPoint(sketch, "E157.visualSharp", {"position": v(-1.02, 16.5) * mm});
            skArc(sketch, "E157.filletArc", {"start": v(-1.02, 17.2) * mm, "mid": v(-0.81, 16.7) * mm, "end": v(-0.32, 16.5) * mm});
            skPoint(sketch, "E158.visualSharp", {"position": v(-1.02, 13.5) * mm});
            skArc(sketch, "E158.filletArc", {"start": v(-0.32, 13.5) * mm, "mid": v(-0.81, 13.3) * mm, "end": v(-1.02, 12.8) * mm});
            skPoint(sketch, "E159.visualSharp", {"position": v(0.78, 16.5) * mm});
            skArc(sketch, "E159.filletArc", {"start": v(0.08, 16.5) * mm, "mid": v(0.58, 16.7) * mm, "end": v(0.78, 17.2) * mm});
            skPoint(sketch, "E160.visualSharp", {"position": v(0.78, 13.5) * mm});
            skArc(sketch, "E160.filletArc", {"start": v(0.78, 12.8) * mm, "mid": v(0.58, 13.3) * mm, "end": v(0.08, 13.5) * mm});
            skPoint(sketch, "E161.visualSharp", {"position": v(5.98, 16.5) * mm});
            skArc(sketch, "E161.filletArc", {"start": v(5.98, 17.2) * mm, "mid": v(6.19, 16.7) * mm, "end": v(6.68, 16.5) * mm});
            skPoint(sketch, "E162.visualSharp", {"position": v(5.98, 13.5) * mm});
            skArc(sketch, "E162.filletArc", {"start": v(6.68, 13.5) * mm, "mid": v(6.19, 13.3) * mm, "end": v(5.98, 12.8) * mm});
            skPoint(sketch, "E163.visualSharp", {"position": v(7.78, 16.5) * mm});
            skArc(sketch, "E163.filletArc", {"start": v(7.08, 16.5) * mm, "mid": v(7.58, 16.7) * mm, "end": v(7.78, 17.2) * mm});
            skPoint(sketch, "E164.visualSharp", {"position": v(7.78, 13.5) * mm});
            skArc(sketch, "E164.filletArc", {"start": v(7.78, 12.8) * mm, "mid": v(7.58, 13.3) * mm, "end": v(7.08, 13.5) * mm});
            skSolve(sketch);
        }
        {
            var Q0;
            Q0=makeQuery(id+"F7.imprint","IMPRINT",FACE,{"disambiguationData":[TD([[makeQuery(id+"F7.imprint","IMPRINT",EDGE,{"derivedFrom":sQuery(id+"F7.wireOp",EDGE,"UmTU5QJp-7VUr-Rgx0-PGNT-urwNqFAXSblL.bottom")}),-1.0]])]});
            var Q1;
            Q1=makeQuery(id+"F7.imprint","IMPRINT",FACE,{"disambiguationData":[TD([[makeQuery(id+"F7.imprint","IMPRINT",EDGE,{"derivedFrom":sQuery(id+"F7.wireOp",EDGE,"rtgu5TSf-RkWG-K3Mp-yo34-yN2Fgp7kvYir.bottom")}),-1.0]])]});
            var Q2;
            Q2=makeQuery(id+"F7.imprint","IMPRINT",FACE,{"disambiguationData":[TD([[makeQuery(id+"F7.imprint","IMPRINT",EDGE,{"derivedFrom":sQuery(id+"F7.wireOp",EDGE,"o0F86HP2-MkUC-ZLcD-2GUC-Z4yFupaMk3gY.bottom")}),-1.0]])]});
            var Q3;
            Q3=makeQuery(id+"F7.imprint","IMPRINT",FACE,{"disambiguationData":[TD([[makeQuery(id+"F7.imprint","IMPRINT",EDGE,{"derivedFrom":sQuery(id+"F7.wireOp",EDGE,"2pmgMrIP-hSHB-vqD5-GrqW-QgvnTVbeCV0Q.bottom")}),-1.0]])]});
            var Q4;
            Q4=makeQuery(id+"F7.imprint","IMPRINT",FACE,{"disambiguationData":[TD([[makeQuery(id+"F7.imprint","IMPRINT",EDGE,{"derivedFrom":sQuery(id+"F7.wireOp",EDGE,"7FuP1ydS-W3tj-HnwQ-QVNf-xIVtqxvrDFHr.bottom")}),1.0]])]});
            var Q5;
            {var subQ0=sQuery(id+"F7.wireOp",EDGE,"2WOX9ifT-60zd-DsnJ-6w09-qQr31wYuHzVq");Q5=makeQuery(id+"F7.imprint","IMPRINT",FACE,{"disambiguationData":[TD([[makeQuery(id+"F7.imprint","IMPRINT",EDGE,{"derivedFrom":subQ0}),-1.0]])]});}
            var Q6;
            {var subQ1=sQuery(id+"F7.wireOp",EDGE,"E63");Q6=makeQuery(id+"F7.imprint","IMPRINT",FACE,{"disambiguationData":[TD([[makeQuery(id+"F7.imprint","IMPRINT",EDGE,{"derivedFrom":subQ1}),1.0]])]});}
            var Q7;
            {var subQ0=sQuery(id+"F7.wireOp",EDGE,"udRqoa8R-MnVj-7dwP-uXg2-csblUBrv88u4");Q7=makeQuery(id+"F7.imprint","IMPRINT",FACE,{"disambiguationData":[TD([[makeQuery(id+"F7.imprint","IMPRINT",EDGE,{"derivedFrom":subQ0}),1.0]])]});}
            var Q8;
            {var subQ0=sQuery(id+"F7.wireOp",EDGE,"Y5pypZQJ-bgb1-zOfl-DvE0-baqu0DW36QP2");Q8=makeQuery(id+"F7.imprint","IMPRINT",FACE,{"disambiguationData":[TD([[makeQuery(id+"F7.imprint","IMPRINT",EDGE,{"derivedFrom":subQ0}),1.0]])]});}
            var Q9;
            {var subQ0=sQuery(id+"F7.wireOp",EDGE,"nVUh7NYb-BNTa-lWt2-VIeA-7NCzMtkfgAhI");Q9=makeQuery(id+"F7.imprint","IMPRINT",FACE,{"disambiguationData":[TD([[makeQuery(id+"F7.imprint","IMPRINT",EDGE,{"derivedFrom":subQ0}),1.0]])]});}
            var Q10;
            Q10=makeQuery(id+"F7.imprint","IMPRINT",FACE,{"disambiguationData":[TD([[makeQuery(id+"F7.imprint","IMPRINT",EDGE,{"derivedFrom":sQuery(id+"F7.wireOp",EDGE,"E101.MirrorCS")}),-1.0]])]});
            var Q11;
            Q11=makeQuery(id+"F7.imprint","IMPRINT",FACE,{"disambiguationData":[TD([[makeQuery(id+"F7.imprint","IMPRINT",EDGE,{"derivedFrom":sQuery(id+"F7.wireOp",EDGE,"E96.MirrorCS")}),1.0]])]});
            var Q12;
            Q12=makeQuery(id+"F7.imprint","IMPRINT",FACE,{"disambiguationData":[TD([[makeQuery(id+"F7.imprint","IMPRINT",EDGE,{"derivedFrom":sQuery(id+"F7.wireOp",EDGE,"E108.MirrorCS")}),1.0]])]});
            var Q13;
            Q13=makeQuery(id+"F7.imprint","IMPRINT",FACE,{"disambiguationData":[TD([[makeQuery(id+"F7.imprint","IMPRINT",EDGE,{"derivedFrom":sQuery(id+"F7.wireOp",EDGE,"E95.MirrorCS")}),-1.0]])]});
            var Q14;
            Q14=makeQuery(id+"F7.imprint","IMPRINT",FACE,{"disambiguationData":[TD([[makeQuery(id+"F7.imprint","IMPRINT",EDGE,{"derivedFrom":sQuery(id+"F7.wireOp",EDGE,"E99.MirrorCS")}),1.0]])]});
            var Q15;
            Q15=makeQuery(id+"F7.imprint","IMPRINT",FACE,{"disambiguationData":[TD([[makeQuery(id+"F7.imprint","IMPRINT",EDGE,{"derivedFrom":sQuery(id+"F7.wireOp",EDGE,"E64.bottom")}),1.0]])]});
            var Q16;
            Q16=makeQuery(id+"F7.imprint","IMPRINT",FACE,{"disambiguationData":[TD([[makeQuery(id+"F7.imprint","IMPRINT",EDGE,{"derivedFrom":sQuery(id+"F7.wireOp",EDGE,"E65.bottom")}),-1.0]])]});
            var Q17;
            Q17=makeQuery(id+"F7.imprint","IMPRINT",FACE,{"disambiguationData":[TD([[makeQuery(id+"F7.imprint","IMPRINT",EDGE,{"derivedFrom":sQuery(id+"F7.wireOp",EDGE,"E66.bottom")}),1.0]])]});
            var Q18;
            Q18=makeQuery(id+"F7.imprint","IMPRINT",FACE,{"disambiguationData":[TD([[makeQuery(id+"F7.imprint","IMPRINT",EDGE,{"derivedFrom":sQuery(id+"F7.wireOp",EDGE,"E67.bottom")}),1.0]])]});
            var Q19;
            Q19=makeQuery(id+"F7.imprint","IMPRINT",FACE,{"disambiguationData":[TD([[makeQuery(id+"F7.imprint","IMPRINT",EDGE,{"derivedFrom":sQuery(id+"F7.wireOp",EDGE,"E68.bottom")}),1.0]])]});
            var Q20;
            Q20=makeQuery(id+"F7.imprint","IMPRINT",FACE,{"disambiguationData":[TD([[makeQuery(id+"F7.imprint","IMPRINT",EDGE,{"derivedFrom":sQuery(id+"F7.wireOp",EDGE,"E91.bottom")}),-1.0]])]});
            var Q21;
            Q21=makeQuery(id+"F7.imprint","IMPRINT",FACE,{"disambiguationData":[TD([[makeQuery(id+"F7.imprint","IMPRINT",EDGE,{"derivedFrom":sQuery(id+"F7.wireOp",EDGE,"E92.bottom")}),-1.0]])]});
            var Q22;
            Q22=makeQuery(id+"F7.imprint","IMPRINT",FACE,{"disambiguationData":[TD([[makeQuery(id+"F7.imprint","IMPRINT",EDGE,{"derivedFrom":sQuery(id+"F7.wireOp",EDGE,"E93.bottom")}),-1.0]])]});
            var Q23;
            Q23=makeQuery(id+"F7.imprint","IMPRINT",FACE,{"disambiguationData":[TD([[makeQuery(id+"F7.imprint","IMPRINT",EDGE,{"derivedFrom":sQuery(id+"F7.wireOp",EDGE,"E94.bottom")}),-1.0]])]});
            var Q24;
            Q24=makeQuery(id+"F7.imprint","IMPRINT",FACE,{"disambiguationData":[TD([[makeQuery(id+"F7.imprint","IMPRINT",EDGE,{"derivedFrom":sQuery(id+"F7.wireOp",EDGE,"E90.bottom")}),-1.0]])]});
            var Q25;
            {var subQ0=sQuery(id+"F7.wireOp",EDGE,"E120.left");Q25=makeQuery(id+"F7.imprint","IMPRINT",FACE,{"disambiguationData":[TD([[makeQuery(id+"F7.imprint","IMPRINT",EDGE,{"derivedFrom":subQ0}),1.0]])]});}
            var Q26;
            {var subQ1=sQuery(id+"F7.wireOp",EDGE,"E120.bottom");Q26=makeQuery(id+"F7.imprint","IMPRINT",FACE,{"disambiguationData":[TD([[makeQuery(id+"F7.imprint","IMPRINT",EDGE,{"derivedFrom":subQ1}),-1.0]])]});}
            var Q27;
            Q27=makeQuery(id+"F7.imprint","IMPRINT",FACE,{"disambiguationData":[TD([[makeQuery(id+"F7.imprint","IMPRINT",EDGE,{"derivedFrom":sQuery(id+"F7.wireOp",EDGE,"E68.top")}),-1.0]])]});
            var Q28;
            Q28=makeQuery(id+"F7.imprint","IMPRINT",FACE,{"disambiguationData":[TD([[makeQuery(id+"F7.imprint","IMPRINT",EDGE,{"derivedFrom":sQuery(id+"F7.wireOp",EDGE,"E67.top")}),-1.0]])]});
            var Q29;
            Q29=makeQuery(id+"F7.imprint","IMPRINT",FACE,{"disambiguationData":[TD([[makeQuery(id+"F7.imprint","IMPRINT",EDGE,{"derivedFrom":sQuery(id+"F7.wireOp",EDGE,"E66.top")}),-1.0]])]});
            var Q30;
            Q30=makeQuery(id+"F7.imprint","IMPRINT",FACE,{"disambiguationData":[TD([[makeQuery(id+"F7.imprint","IMPRINT",EDGE,{"derivedFrom":sQuery(id+"F7.wireOp",EDGE,"E65.top")}),1.0]])]});
            var Q31;
            Q31=makeQuery(id+"F7.imprint","IMPRINT",FACE,{"disambiguationData":[TD([[makeQuery(id+"F7.imprint","IMPRINT",EDGE,{"derivedFrom":sQuery(id+"F7.wireOp",EDGE,"E64.top")}),-1.0]])]});
            extrude(context, id + "F8", {"entities" : qUnion([Q0, Q1, Q2, Q3, Q4, Q5, Q6, Q7, Q8, Q9, Q10, Q11, Q12, Q13, Q14, Q15, Q16, Q17, Q18, Q19, Q20, Q21, Q22, Q23, Q24, Q25, Q26, Q27, Q28, Q29, Q30, Q31]), "operationType" : NewBodyOperationType.REMOVE, "endBound" : BoundingType.SYMMETRIC, "oppositeDirection" : true, "depth" : 10 * mm, "offsetDistance" : 25 * mm});
        }
    });
